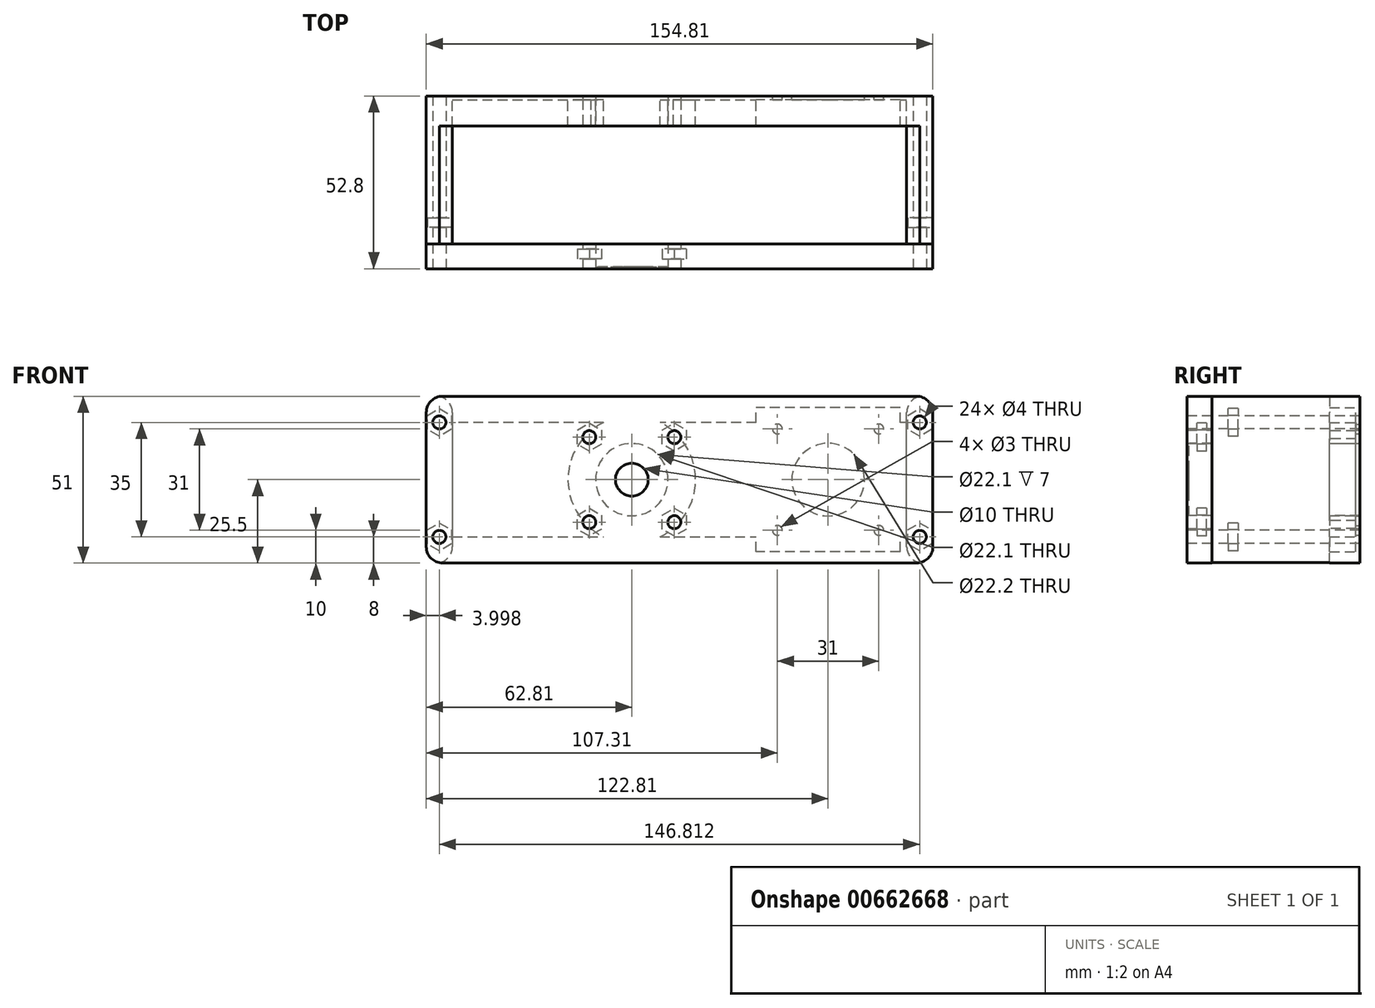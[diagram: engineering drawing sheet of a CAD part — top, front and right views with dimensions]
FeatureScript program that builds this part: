
annotation { "Feature Type Name" : "Feature", "Feature Type Description" : "" }
export const myFeature = defineFeature(function(context is Context, id is Id, definition is map)
    precondition{}
    {
        {
            var Q0;
            Q0=qCreatedBy(makeId("Front.planeOp"),FACE);
            var sketch = newSketch(context, id + "F0", { "sketchPlane" : qUnion([Q0])});
            skCircle(sketch, "E0", {"center": v(0, 0) * mm, "radius": 11.05 * mm});
            skCircle(sketch, "E1", {"center": v(60, 0) * mm, "radius": 11.1 * mm});
            skLineSegment(sketch, "E2.bottom", {"start": v(75.5, -15.5) * mm, "end": v(44.5, -15.5) * mm, "construction": true});
            skLineSegment(sketch, "E2.top", {"start": v(75.5, 15.5) * mm, "end": v(44.5, 15.5) * mm, "construction": true});
            skLineSegment(sketch, "E2.left", {"start": v(75.5, -15.5) * mm, "end": v(75.5, 15.5) * mm, "construction": true});
            skLineSegment(sketch, "E2.right", {"start": v(44.5, -15.5) * mm, "end": v(44.5, 15.5) * mm, "construction": true});
            skCircle(sketch, "E3", {"center": v(44.5, 15.5) * mm, "radius": 1.5 * mm});
            skCircle(sketch, "E4", {"center": v(75.5, 15.5) * mm, "radius": 1.5 * mm});
            skCircle(sketch, "E5", {"center": v(75.5, -15.5) * mm, "radius": 1.5 * mm});
            skCircle(sketch, "E6", {"center": v(44.5, -15.5) * mm, "radius": 1.5 * mm});
            skLineSegment(sketch, "E7.bottom", {"start": v(-62.81, 25.5) * mm, "end": v(92, 25.5) * mm});
            skLineSegment(sketch, "E7.top", {"start": v(-62.81, -25.5) * mm, "end": v(92, -25.5) * mm});
            skLineSegment(sketch, "E7.left", {"start": v(-62.81, 25.5) * mm, "end": v(-62.81, -25.5) * mm});
            skLineSegment(sketch, "E7.right", {"start": v(92, 25.5) * mm, "end": v(92, -25.5) * mm});
            skCircle(sketch, "E8", {"center": v(0, 0) * mm, "radius": 47.81 * mm, "construction": true});
            skCircle(sketch, "E9", {"center": v(60, 0) * mm, "radius": 12.19 * mm, "construction": true});
            skCircle(sketch, "E10", {"center": v(0, 0) * mm, "radius": 5 * mm});
            skSolve(sketch);
        }
        {
            var Q0;
            Q0=makeQuery(id+"F0.imprint","IMPRINT",FACE,{"disambiguationData":[TD([[makeQuery(id+"F0.imprint","IMPRINT",EDGE,{"derivedFrom":sQuery(id+"F0.wireOp",EDGE,"E0")}),-1.0]])]});
            extrude(context, id + "F1", {"entities" : qUnion([Q0]), "depth" : 1.2 * mm});
        }
        {
            var Q0;
            Q0=makeQuery(id+"F1.opExtrude","CAP_FACE",FACE,{"disambiguationData":[OSD([sQuery(id+"F0.wireOp",EDGE,"E0"),sQuery(id+"F0.wireOp",EDGE,"E1"),sQuery(id+"F0.wireOp",EDGE,"E3"),sQuery(id+"F0.wireOp",EDGE,"E4"),sQuery(id+"F0.wireOp",EDGE,"E5"),sQuery(id+"F0.wireOp",EDGE,"E6"),sQuery(id+"F0.wireOp",EDGE,"E7.bottom"),sQuery(id+"F0.wireOp",EDGE,"E7.top"),sQuery(id+"F0.wireOp",EDGE,"E7.left"),sQuery(id+"F0.wireOp",EDGE,"E7.right")])],"isStart":false});
            var sketch = newSketch(context, id + "F2", { "sketchPlane" : qUnion([Q0])});
            skLineSegment(sketch, "E11.0", {"start": v(84, 17.5) * mm, "end": v(82, 17.5) * mm});
            skLineSegment(sketch, "E11.1", {"start": v(84, -17.5) * mm, "end": v(84, 17.5) * mm});
            skLineSegment(sketch, "E11.2", {"start": v(-54.81, -17.5) * mm, "end": v(-8.6, -17.5) * mm});
            skLineSegment(sketch, "E11.3", {"start": v(-54.81, 17.5) * mm, "end": v(-54.81, -17.5) * mm});
            skArc(sketch, "E12", {"start": v(8.6, -17.5) * mm, "mid": v(19.5, 0) * mm, "end": v(8.6, 17.5) * mm});
            skLineSegment(sketch, "E13.trimOffspring", {"start": v(8.6, -17.5) * mm, "end": v(38, -17.5) * mm});
            skLineSegment(sketch, "E14.trimOffspring", {"start": v(-8.6, 17.5) * mm, "end": v(-54.81, 17.5) * mm});
            skArc(sketch, "E15.trimOffspring", {"start": v(-8.6, 17.5) * mm, "mid": v(-19.5, 0) * mm, "end": v(-8.6, -17.5) * mm});
            skLineSegment(sketch, "E16.bottom", {"start": v(82, -22) * mm, "end": v(38, -22) * mm});
            skLineSegment(sketch, "E16.top", {"start": v(82, 22) * mm, "end": v(38, 22) * mm});
            skLineSegment(sketch, "E16.left", {"start": v(82, -22) * mm, "end": v(82, 22) * mm});
            skLineSegment(sketch, "E16.right", {"start": v(38, -22) * mm, "end": v(38, 22) * mm});
            skPoint(sketch, "E16.middle", {"position": v(60, 0) * mm});
            skLineSegment(sketch, "E17.trimOffspring", {"start": v(38, 17.5) * mm, "end": v(8.6, 17.5) * mm});
            skLineSegment(sketch, "E18.trimOffspring", {"start": v(82, -17.5) * mm, "end": v(84, -17.5) * mm});
            skSolve(sketch);
        }
        {
            var Q0;
            Q0=makeQuery(id+"F2.imprint","IMPRINT",FACE,{"disambiguationData":[TD([[makeQuery(id+"F2.imprint","IMPRINT",EDGE,{"derivedFrom":sQuery(id+"F2.wireOp",EDGE,"E11.0")}),-1.0]])]});
            extrude(context, id + "F3", {"entities" : qUnion([Q0]), "operationType" : NewBodyOperationType.ADD, "depth" : 8 * mm});
        }
        {
            var Q0;
            Q0=makeQuery(id+"F3.opExtrude","CAP_FACE",FACE,{"disambiguationData":[OSD([sQuery(id+"F0.wireOp",EDGE,"E0"),sQuery(id+"F0.wireOp",EDGE,"E7.bottom"),sQuery(id+"F0.wireOp",EDGE,"E7.top"),sQuery(id+"F0.wireOp",EDGE,"E7.left"),sQuery(id+"F0.wireOp",EDGE,"E7.right"),sQuery(id+"F2.wireOp",EDGE,"E11.0"),sQuery(id+"F2.wireOp",EDGE,"E11.1"),sQuery(id+"F2.wireOp",EDGE,"E11.2"),sQuery(id+"F2.wireOp",EDGE,"E11.3"),sQuery(id+"F2.wireOp",EDGE,"E12"),sQuery(id+"F2.wireOp",EDGE,"E13.trimOffspring"),sQuery(id+"F2.wireOp",EDGE,"E14.trimOffspring"),sQuery(id+"F2.wireOp",EDGE,"E15.trimOffspring")])],"isStart":false});
            var sketch = newSketch(context, id + "F4", { "sketchPlane" : qUnion([Q0])});
            skLineSegment(sketch, "E19.bottom", {"start": v(92, -25.5) * mm, "end": v(84, -25.5) * mm});
            skLineSegment(sketch, "E19.top", {"start": v(92, 25.5) * mm, "end": v(84, 25.5) * mm});
            skLineSegment(sketch, "E19.left", {"start": v(92, -25.5) * mm, "end": v(92, 25.5) * mm});
            skLineSegment(sketch, "E19.right", {"start": v(84, -25.5) * mm, "end": v(84, 25.5) * mm});
            skLineSegment(sketch, "E20.bottom", {"start": v(-62.81, -25.5) * mm, "end": v(-54.81, -25.5) * mm});
            skLineSegment(sketch, "E20.top", {"start": v(-62.81, 25.5) * mm, "end": v(-54.81, 25.5) * mm});
            skLineSegment(sketch, "E20.left", {"start": v(-62.81, -25.5) * mm, "end": v(-62.81, 25.5) * mm});
            skLineSegment(sketch, "E20.right", {"start": v(-54.81, -25.5) * mm, "end": v(-54.81, 25.5) * mm});
            skSolve(sketch);
        }
        {
            var Q0;
            Q0=qSketchRegion(id+"F4",true);
            extrude(context, id + "F5", {"entities" : qUnion([Q0]), "operationType" : NewBodyOperationType.ADD, "depth" : 36 * mm});
        }
        {
            var Q0;
            Q0=makeQuery(id+"F5.opExtrude","CAP_FACE",FACE,{"disambiguationData":[OSD([sQuery(id+"F4.wireOp",EDGE,"E20.bottom"),sQuery(id+"F4.wireOp",EDGE,"E20.top"),sQuery(id+"F4.wireOp",EDGE,"E20.left"),sQuery(id+"F4.wireOp",EDGE,"E20.right")])],"isStart":false});
            var sketch = newSketch(context, id + "F6", { "sketchPlane" : qUnion([Q0])});
            skLineSegment(sketch, "E21.0.2", {"start": v(92, -25.5) * mm, "end": v(92, 25.5) * mm});
            skLineSegment(sketch, "E22.0", {"start": v(-62.81, 25.5) * mm, "end": v(-62.81, -25.5) * mm});
            skLineSegment(sketch, "E23", {"start": v(-62.81, -25.5) * mm, "end": v(92, -25.5) * mm});
            skLineSegment(sketch, "E24", {"start": v(-62.81, 25.5) * mm, "end": v(92, 25.5) * mm});
            skSolve(sketch);
        }
        {
            var Q0;
            Q0=qSketchRegion(id+"F6",true);
            extrude(context, id + "F7", {"entities" : qUnion([Q0]), "depth" : 7.6 * mm});
        }
        {
            var Q0;
            Q0=makeQuery(id+"F0.imprint","IMPRINT",FACE,{"disambiguationData":[TD([[makeQuery(id+"F0.imprint","IMPRINT",EDGE,{"derivedFrom":sQuery(id+"F0.wireOp",EDGE,"E0")}),1.0]])]});
            extrude(context, id + "F8", {"entities" : qUnion([Q0]), "operationType" : NewBodyOperationType.ADD, "depth" : .6 * mm});
        }
        {
            var Q0;
            Q0=makeQuery(id+"F7.opExtrude","CAP_FACE",FACE,{"disambiguationData":[OSD([sQuery(id+"F6.wireOp",EDGE,"E21.0.2"),sQuery(id+"F6.wireOp",EDGE,"E22.0"),sQuery(id+"F6.wireOp",EDGE,"E23"),sQuery(id+"F6.wireOp",EDGE,"E24")])],"isStart":false});
            var sketch = newSketch(context, id + "F9", { "sketchPlane" : qUnion([Q0])});
            skCircle(sketch, "E25.0", {"center": v(0, 0) * mm, "radius": 11.05 * mm});
            skCircle(sketch, "E26.0", {"center": v(0, 0) * mm, "radius": 5 * mm});
            skLineSegment(sketch, "E27.bottom", {"start": v(13, -13) * mm, "end": v(-13, -13) * mm, "construction": true});
            skLineSegment(sketch, "E27.top", {"start": v(13, 13) * mm, "end": v(-13, 13) * mm, "construction": true});
            skLineSegment(sketch, "E27.left", {"start": v(13, -13) * mm, "end": v(13, 13) * mm, "construction": true});
            skLineSegment(sketch, "E27.right", {"start": v(-13, -13) * mm, "end": v(-13, 13) * mm, "construction": true});
            skCircle(sketch, "E28", {"center": v(-13, -13) * mm, "radius": 2 * mm});
            skCircle(sketch, "E29", {"center": v(13, -13) * mm, "radius": 2 * mm});
            skCircle(sketch, "E30", {"center": v(13, 13) * mm, "radius": 2 * mm});
            skCircle(sketch, "E31", {"center": v(-13, 13) * mm, "radius": 2 * mm});
            skSolve(sketch);
        }
        {
            var Q0;
            Q0=qSketchRegion(id+"F9",true);
            var Q1;
            Q1=makeQuery(id+"F9.imprint","IMPRINT",FACE,{"disambiguationData":[TD([[makeQuery(id+"F9.imprint","IMPRINT",EDGE,{"derivedFrom":sQuery(id+"F9.wireOp",EDGE,"E25.0")}),1.0]])]});
            var Q2;
            Q2=makeQuery(id+"F9.imprint","IMPRINT",FACE,{"disambiguationData":[TD([[makeQuery(id+"F9.imprint","IMPRINT",EDGE,{"derivedFrom":sQuery(id+"F9.wireOp",EDGE,"E26.0")}),1.0]])]});
            extrude(context, id + "F10", {"entities" : qUnion([Q0, Q1, Q2]), "operationType" : NewBodyOperationType.REMOVE, "endBound" : BoundingType.THROUGH_ALL, "oppositeDirection" : true, "depth" : 25 * mm});
        }
        {
            var Q0;
            Q0=makeQuery(id+"F9.imprint","IMPRINT",FACE,{"disambiguationData":[TD([[makeQuery(id+"F9.imprint","IMPRINT",EDGE,{"derivedFrom":sQuery(id+"F9.wireOp",EDGE,"E25.0")}),1.0]])]});
            extrude(context, id + "F11", {"entities" : qUnion([Q0]), "operationType" : NewBodyOperationType.ADD, "oppositeDirection" : true, "depth" : .6 * mm});
        }
        {
            var Q0;
            Q0=makeQuery(id+"F9.imprint","IMPRINT",FACE,{"disambiguationData":[TD([[makeQuery(id+"F9.imprint","IMPRINT",EDGE,{"derivedFrom":sQuery(id+"F9.wireOp",EDGE,"E25.0")}),-1.0]])]});
            cPlane(context, id + "F12", {"entities" : qUnion([Q0]), "cplaneType" : CPlaneType.OFFSET, "offset" : 3 * mm, "oppositeDirection" : true, "width" : 150 * mm, "height" : 150 * mm});
        }
        {
            var Q0;
            Q0=qCreatedBy(id+"F12.planeOp",FACE);
            var sketch = newSketch(context, id + "F13", { "sketchPlane" : qUnion([Q0])});
            skLineSegment(sketch, "E32.0", {"start": v(13, -13) * mm, "end": v(-13, -13) * mm, "construction": true});
            skLineSegment(sketch, "E33.0", {"start": v(-13, -13) * mm, "end": v(-13, 13) * mm, "construction": true});
            skLineSegment(sketch, "E34.0", {"start": v(13, 13) * mm, "end": v(-13, 13) * mm, "construction": true});
            skLineSegment(sketch, "E35.0", {"start": v(13, -13) * mm, "end": v(13, 13) * mm, "construction": true});
            skCircle(sketch, "E36.cCircle", {"center": v(-13, -13) * mm, "radius": 3.7 * mm, "construction": true});
            skLineSegment(sketch, "E36.0", {"start": v(-9.3, -10.86) * mm, "end": v(-9.3, -15.14) * mm});
            skLineSegment(sketch, "E36.1", {"start": v(-9.3, -15.14) * mm, "end": v(-13, -17.27) * mm});
            skLineSegment(sketch, "E36.2", {"start": v(-13, -17.27) * mm, "end": v(-16.7, -15.14) * mm});
            skLineSegment(sketch, "E36.3", {"start": v(-16.7, -15.14) * mm, "end": v(-16.7, -10.86) * mm});
            skLineSegment(sketch, "E36.4", {"start": v(-16.7, -10.86) * mm, "end": v(-13, -8.73) * mm});
            skLineSegment(sketch, "E36.5", {"start": v(-13, -8.73) * mm, "end": v(-9.3, -10.86) * mm});
            skPoint(sketch, "E36.0.midPoint", {"position": v(-9.3, -13) * mm});
            skCircle(sketch, "E37.cCircle", {"center": v(-13, 13) * mm, "radius": 3.7 * mm, "construction": true});
            skLineSegment(sketch, "E37.0", {"start": v(-9.3, 15.14) * mm, "end": v(-9.3, 10.86) * mm});
            skLineSegment(sketch, "E37.1", {"start": v(-9.3, 10.86) * mm, "end": v(-13, 8.73) * mm});
            skLineSegment(sketch, "E37.2", {"start": v(-13, 8.73) * mm, "end": v(-16.7, 10.86) * mm});
            skLineSegment(sketch, "E37.3", {"start": v(-16.7, 10.86) * mm, "end": v(-16.7, 15.14) * mm});
            skLineSegment(sketch, "E37.4", {"start": v(-16.7, 15.14) * mm, "end": v(-13, 17.27) * mm});
            skLineSegment(sketch, "E37.5", {"start": v(-13, 17.27) * mm, "end": v(-9.3, 15.14) * mm});
            skPoint(sketch, "E37.0.midPoint", {"position": v(-9.3, 13) * mm});
            skCircle(sketch, "E38.cCircle", {"center": v(13, 13) * mm, "radius": 3.7 * mm, "construction": true});
            skLineSegment(sketch, "E38.0", {"start": v(9.3, 10.86) * mm, "end": v(9.3, 15.14) * mm});
            skLineSegment(sketch, "E38.1", {"start": v(9.3, 15.14) * mm, "end": v(13, 17.27) * mm});
            skLineSegment(sketch, "E38.2", {"start": v(13, 17.27) * mm, "end": v(16.7, 15.14) * mm});
            skLineSegment(sketch, "E38.3", {"start": v(16.7, 15.14) * mm, "end": v(16.7, 10.86) * mm});
            skLineSegment(sketch, "E38.4", {"start": v(16.7, 10.86) * mm, "end": v(13, 8.73) * mm});
            skLineSegment(sketch, "E38.5", {"start": v(13, 8.73) * mm, "end": v(9.3, 10.86) * mm});
            skPoint(sketch, "E38.0.midPoint", {"position": v(9.3, 13) * mm});
            skCircle(sketch, "E39.cCircle", {"center": v(13, -13) * mm, "radius": 3.7 * mm, "construction": true});
            skLineSegment(sketch, "E39.0", {"start": v(9.3, -15.14) * mm, "end": v(9.3, -10.86) * mm});
            skLineSegment(sketch, "E39.1", {"start": v(9.3, -10.86) * mm, "end": v(13, -8.73) * mm});
            skLineSegment(sketch, "E39.2", {"start": v(13, -8.73) * mm, "end": v(16.7, -10.86) * mm});
            skLineSegment(sketch, "E39.3", {"start": v(16.7, -10.86) * mm, "end": v(16.7, -15.14) * mm});
            skLineSegment(sketch, "E39.4", {"start": v(16.7, -15.14) * mm, "end": v(13, -17.27) * mm});
            skLineSegment(sketch, "E39.5", {"start": v(13, -17.27) * mm, "end": v(9.3, -15.14) * mm});
            skPoint(sketch, "E39.0.midPoint", {"position": v(9.3, -13) * mm});
            skSolve(sketch);
        }
        {
            var Q0;
            Q0=qSketchRegion(id+"F13",true);
            extrude(context, id + "F14", {"entities" : qUnion([Q0]), "operationType" : NewBodyOperationType.REMOVE, "oppositeDirection" : true, "depth" : 3 * mm});
        }
        {
            var Q0;
            Q0=makeQuery(id+"F5.opExtrude","CAP_FACE",FACE,{"disambiguationData":[OSD([sQuery(id+"F4.wireOp",EDGE,"E20.bottom"),sQuery(id+"F4.wireOp",EDGE,"E20.top"),sQuery(id+"F4.wireOp",EDGE,"E20.left"),sQuery(id+"F4.wireOp",EDGE,"E20.right")])],"isStart":false});
            var sketch = newSketch(context, id + "F15", { "sketchPlane" : qUnion([Q0])});
            skLineSegment(sketch, "E40.0.0", {"start": v(84, 25.5) * mm, "end": v(84, -25.5) * mm, "construction": true});
            skLineSegment(sketch, "E40.0.1", {"start": v(84, -25.5) * mm, "end": v(92, -25.5) * mm, "construction": true});
            skLineSegment(sketch, "E40.0.2", {"start": v(92, -25.5) * mm, "end": v(92, 25.5) * mm, "construction": true});
            skLineSegment(sketch, "E40.0.3", {"start": v(92, 25.5) * mm, "end": v(84, 25.5) * mm, "construction": true});
            skLineSegment(sketch, "E41", {"start": v(-58.81, -25.5) * mm, "end": v(-58.81, 25.5) * mm, "construction": true});
            skLineSegment(sketch, "E42", {"start": v(88, -25.5) * mm, "end": v(88, 25.5) * mm, "construction": true});
            skCircle(sketch, "E43", {"center": v(88, 17.5) * mm, "radius": 2 * mm});
            skCircle(sketch, "E44", {"center": v(88, -17.5) * mm, "radius": 2 * mm});
            skCircle(sketch, "E45", {"center": v(-58.81, 17.5) * mm, "radius": 2 * mm});
            skCircle(sketch, "E46", {"center": v(-58.81, -17.5) * mm, "radius": 2 * mm});
            skSolve(sketch);
        }
        {
            var Q0;
            Q0=qSketchRegion(id+"F15",true);
            extrude(context, id + "F16", {"entities" : qUnion([Q0]), "operationType" : NewBodyOperationType.REMOVE, "oppositeDirection" : true, "depth" : 15 * mm});
        }
        {
            var Q0;
            Q0=makeQuery(id+"F15.imprint","IMPRINT",FACE,{"disambiguationData":[TD([[makeQuery(id+"F15.imprint","IMPRINT",EDGE,{"derivedFrom":sQuery(id+"F15.wireOp",EDGE,"E45")}),-1.0]])]});
            cPlane(context, id + "F17", {"entities" : qUnion([Q0]), "cplaneType" : CPlaneType.OFFSET, "offset" : 5 * mm, "oppositeDirection" : true, "width" : 150 * mm, "height" : 150 * mm});
        }
        {
            var Q0;
            Q0=qCreatedBy(id+"F17.planeOp",FACE);
            var sketch = newSketch(context, id + "F18", { "sketchPlane" : qUnion([Q0])});
            skPoint(sketch, "E47.0", {"position": v(-58.81, -17.5) * mm});
            skPoint(sketch, "E48.0", {"position": v(-58.81, 17.5) * mm});
            skPoint(sketch, "E49.0", {"position": v(88, -17.5) * mm});
            skPoint(sketch, "E50.0", {"position": v(88, 17.5) * mm});
            skCircle(sketch, "E51.cCircle", {"center": v(-58.81, 17.5) * mm, "radius": 3.7 * mm, "construction": true});
            skLineSegment(sketch, "E51.0", {"start": v(-55.11, 19.64) * mm, "end": v(-55.11, 15.36) * mm});
            skLineSegment(sketch, "E51.1", {"start": v(-55.11, 15.36) * mm, "end": v(-58.81, 13.23) * mm});
            skLineSegment(sketch, "E51.2", {"start": v(-58.81, 13.23) * mm, "end": v(-62.51, 15.36) * mm});
            skLineSegment(sketch, "E51.3", {"start": v(-62.51, 15.36) * mm, "end": v(-62.51, 19.64) * mm});
            skLineSegment(sketch, "E51.4", {"start": v(-62.51, 19.64) * mm, "end": v(-58.81, 21.77) * mm});
            skLineSegment(sketch, "E51.5", {"start": v(-58.81, 21.77) * mm, "end": v(-55.11, 19.64) * mm});
            skPoint(sketch, "E51.0.midPoint", {"position": v(-55.11, 17.5) * mm});
            skCircle(sketch, "E52.cCircle", {"center": v(-58.81, -17.5) * mm, "radius": 3.7 * mm, "construction": true});
            skLineSegment(sketch, "E52.0", {"start": v(-55.11, -15.36) * mm, "end": v(-55.11, -19.64) * mm});
            skLineSegment(sketch, "E52.1", {"start": v(-55.11, -19.64) * mm, "end": v(-58.81, -21.77) * mm});
            skLineSegment(sketch, "E52.2", {"start": v(-58.81, -21.77) * mm, "end": v(-62.51, -19.64) * mm});
            skLineSegment(sketch, "E52.3", {"start": v(-62.51, -19.64) * mm, "end": v(-62.51, -15.36) * mm});
            skLineSegment(sketch, "E52.4", {"start": v(-62.51, -15.36) * mm, "end": v(-58.81, -13.23) * mm});
            skLineSegment(sketch, "E52.5", {"start": v(-58.81, -13.23) * mm, "end": v(-55.11, -15.36) * mm});
            skPoint(sketch, "E52.0.midPoint", {"position": v(-55.11, -17.5) * mm});
            skCircle(sketch, "E53.cCircle", {"center": v(88, 17.5) * mm, "radius": 3.7 * mm, "construction": true});
            skLineSegment(sketch, "E53.0", {"start": v(84.3, 15.36) * mm, "end": v(84.3, 19.64) * mm});
            skLineSegment(sketch, "E53.1", {"start": v(84.3, 19.64) * mm, "end": v(88, 21.77) * mm});
            skLineSegment(sketch, "E53.2", {"start": v(88, 21.77) * mm, "end": v(91.7, 19.64) * mm});
            skLineSegment(sketch, "E53.3", {"start": v(91.7, 19.64) * mm, "end": v(91.7, 15.36) * mm});
            skLineSegment(sketch, "E53.4", {"start": v(91.7, 15.36) * mm, "end": v(88, 13.23) * mm});
            skLineSegment(sketch, "E53.5", {"start": v(88, 13.23) * mm, "end": v(84.3, 15.36) * mm});
            skPoint(sketch, "E53.0.midPoint", {"position": v(84.3, 17.5) * mm});
            skCircle(sketch, "E54.cCircle", {"center": v(88, -17.5) * mm, "radius": 3.7 * mm, "construction": true});
            skLineSegment(sketch, "E54.0", {"start": v(84.3, -19.64) * mm, "end": v(84.3, -15.36) * mm});
            skLineSegment(sketch, "E54.1", {"start": v(84.3, -15.36) * mm, "end": v(88, -13.23) * mm});
            skLineSegment(sketch, "E54.2", {"start": v(88, -13.23) * mm, "end": v(91.7, -15.36) * mm});
            skLineSegment(sketch, "E54.3", {"start": v(91.7, -15.36) * mm, "end": v(91.7, -19.64) * mm});
            skLineSegment(sketch, "E54.4", {"start": v(91.7, -19.64) * mm, "end": v(88, -21.77) * mm});
            skLineSegment(sketch, "E54.5", {"start": v(88, -21.77) * mm, "end": v(84.3, -19.64) * mm});
            skPoint(sketch, "E54.0.midPoint", {"position": v(84.3, -17.5) * mm});
            skSolve(sketch);
        }
        {
            var Q0;
            Q0=qSketchRegion(id+"F18",true);
            extrude(context, id + "F19", {"entities" : qUnion([Q0]), "operationType" : NewBodyOperationType.REMOVE, "oppositeDirection" : true, "depth" : 3 * mm});
        }
        {
            var Q0;
            Q0=makeQuery(id+"F11.boolean.opBoolean","MERGE",FACE,{"derivedFrom":[makeQuery(id+"F7.opExtrude","CAP_FACE",FACE,{"disambiguationData":[OSD([sQuery(id+"F6.wireOp",EDGE,"E21.0.2"),sQuery(id+"F6.wireOp",EDGE,"E22.0"),sQuery(id+"F6.wireOp",EDGE,"E23"),sQuery(id+"F6.wireOp",EDGE,"E24")])],"isStart":false}),makeQuery(id+"F11.opExtrude","CAP_FACE",FACE,{"disambiguationData":[OSD([sQuery(id+"F9.wireOp",EDGE,"E25.0"),sQuery(id+"F9.wireOp",EDGE,"E26.0")])],"isStart":true})]});
            var sketch = newSketch(context, id + "F20", { "sketchPlane" : qUnion([Q0])});
            skCircle(sketch, "E55.0", {"center": v(-58.81, -17.5) * mm, "radius": 2 * mm});
            skCircle(sketch, "E56.0", {"center": v(-58.81, 17.5) * mm, "radius": 2 * mm});
            skCircle(sketch, "E57.0", {"center": v(88, 17.5) * mm, "radius": 2 * mm});
            skCircle(sketch, "E58.0", {"center": v(88, -17.5) * mm, "radius": 2 * mm});
            skSolve(sketch);
        }
        {
            var Q0;
            Q0=qSketchRegion(id+"F20",true);
            extrude(context, id + "F21", {"entities" : qUnion([Q0]), "operationType" : NewBodyOperationType.REMOVE, "endBound" : BoundingType.THROUGH_ALL, "oppositeDirection" : true, "depth" : 25 * mm});
        }
        {
            var Q0;
            {var subQ0=sQuery(id+"F0.wireOp",EDGE,"E7.left");var subQ1=sQuery(id+"F0.wireOp",EDGE,"E7.top");Q0=makeQuery(id+"F5.boolean.opBoolean","MERGE",EDGE,{"derivedFrom":[makeQuery(id+"F3.boolean.opBoolean","MERGE",EDGE,{"derivedFrom":[makeQuery(id+"F1.opExtrude","SWEPT_EDGE",EDGE,{"disambiguationData":[OSD([subQ1,subQ0])]}),makeQuery(id+"F3.opExtrude","SWEPT_EDGE",EDGE,{"disambiguationData":[OSD([subQ1,subQ0])]})]}),makeQuery(id+"F5.opExtrude","SWEPT_EDGE",EDGE,{"disambiguationData":[OSD([sQuery(id+"F4.wireOp",EDGE,"E20.bottom"),sQuery(id+"F4.wireOp",EDGE,"E20.left")])]})]});}
            var Q1;
            Q1=makeQuery(id+"F7.opExtrude","SWEPT_EDGE",EDGE,{"disambiguationData":[OSD([sQuery(id+"F6.wireOp",EDGE,"E22.0"),sQuery(id+"F6.wireOp",EDGE,"E23")])]});
            var Q2;
            Q2=makeQuery(id+"F7.opExtrude","SWEPT_EDGE",EDGE,{"disambiguationData":[OSD([sQuery(id+"F6.wireOp",EDGE,"E22.0"),sQuery(id+"F6.wireOp",EDGE,"E24")])]});
            var Q3;
            {var subQ0=sQuery(id+"F0.wireOp",EDGE,"E7.left");var subQ1=sQuery(id+"F0.wireOp",EDGE,"E7.bottom");Q3=makeQuery(id+"F5.boolean.opBoolean","MERGE",EDGE,{"derivedFrom":[makeQuery(id+"F3.boolean.opBoolean","MERGE",EDGE,{"derivedFrom":[makeQuery(id+"F1.opExtrude","SWEPT_EDGE",EDGE,{"disambiguationData":[OSD([subQ1,subQ0])]}),makeQuery(id+"F3.opExtrude","SWEPT_EDGE",EDGE,{"disambiguationData":[OSD([subQ1,subQ0])]})]}),makeQuery(id+"F5.opExtrude","SWEPT_EDGE",EDGE,{"disambiguationData":[OSD([sQuery(id+"F4.wireOp",EDGE,"E20.top"),sQuery(id+"F4.wireOp",EDGE,"E20.left")])]})]});}
            var Q4;
            Q4=makeQuery(id+"F5.opExtrude","SWEPT_EDGE",EDGE,{"disambiguationData":[OSD([sQuery(id+"F0.wireOp",EDGE,"E7.bottom"),sQuery(id+"F4.wireOp",EDGE,"E20.top"),sQuery(id+"F4.wireOp",EDGE,"E20.right")])]});
            var Q5;
            Q5=makeQuery(id+"F5.opExtrude","SWEPT_EDGE",EDGE,{"disambiguationData":[OSD([sQuery(id+"F0.wireOp",EDGE,"E7.top"),sQuery(id+"F4.wireOp",EDGE,"E20.bottom"),sQuery(id+"F4.wireOp",EDGE,"E20.right")])]});
            var Q6;
            Q6=makeQuery(id+"F5.opExtrude","SWEPT_EDGE",EDGE,{"disambiguationData":[OSD([sQuery(id+"F0.wireOp",EDGE,"E7.top"),sQuery(id+"F4.wireOp",EDGE,"E19.bottom"),sQuery(id+"F4.wireOp",EDGE,"E19.right")])]});
            var Q7;
            {var subQ0=sQuery(id+"F0.wireOp",EDGE,"E7.right");var subQ1=sQuery(id+"F0.wireOp",EDGE,"E7.top");Q7=makeQuery(id+"F5.boolean.opBoolean","MERGE",EDGE,{"derivedFrom":[makeQuery(id+"F3.boolean.opBoolean","MERGE",EDGE,{"derivedFrom":[makeQuery(id+"F1.opExtrude","SWEPT_EDGE",EDGE,{"disambiguationData":[OSD([subQ1,subQ0])]}),makeQuery(id+"F3.opExtrude","SWEPT_EDGE",EDGE,{"disambiguationData":[OSD([subQ1,subQ0])]})]}),makeQuery(id+"F5.opExtrude","SWEPT_EDGE",EDGE,{"disambiguationData":[OSD([sQuery(id+"F4.wireOp",EDGE,"E19.bottom"),sQuery(id+"F4.wireOp",EDGE,"E19.left")])]})]});}
            var Q8;
            Q8=makeQuery(id+"F7.opExtrude","SWEPT_EDGE",EDGE,{"disambiguationData":[OSD([sQuery(id+"F6.wireOp",EDGE,"E21.0.2"),sQuery(id+"F6.wireOp",EDGE,"E23")])]});
            var Q9;
            {var subQ0=sQuery(id+"F0.wireOp",EDGE,"E7.right");var subQ1=sQuery(id+"F0.wireOp",EDGE,"E7.bottom");Q9=makeQuery(id+"F5.boolean.opBoolean","MERGE",EDGE,{"derivedFrom":[makeQuery(id+"F3.boolean.opBoolean","MERGE",EDGE,{"derivedFrom":[makeQuery(id+"F1.opExtrude","SWEPT_EDGE",EDGE,{"disambiguationData":[OSD([subQ1,subQ0])]}),makeQuery(id+"F3.opExtrude","SWEPT_EDGE",EDGE,{"disambiguationData":[OSD([subQ1,subQ0])]})]}),makeQuery(id+"F5.opExtrude","SWEPT_EDGE",EDGE,{"disambiguationData":[OSD([sQuery(id+"F4.wireOp",EDGE,"E19.top"),sQuery(id+"F4.wireOp",EDGE,"E19.left")])]})]});}
            var Q10;
            Q10=makeQuery(id+"F7.opExtrude","SWEPT_EDGE",EDGE,{"disambiguationData":[OSD([sQuery(id+"F6.wireOp",EDGE,"E21.0.2"),sQuery(id+"F6.wireOp",EDGE,"E24")])]});
            var Q11;
            Q11=makeQuery(id+"F5.opExtrude","SWEPT_EDGE",EDGE,{"disambiguationData":[OSD([sQuery(id+"F0.wireOp",EDGE,"E7.bottom"),sQuery(id+"F4.wireOp",EDGE,"E19.top"),sQuery(id+"F4.wireOp",EDGE,"E19.right")])]});
            fillet(context, id + "F22", {"entities" : qUnion([Q0, Q1, Q2, Q3, Q4, Q5, Q6, Q7, Q8, Q9, Q10, Q11]), "radius" : 5 * mm, "tangentPropagation" : true, "allowEdgeOverflow" : false});
        }
    });
